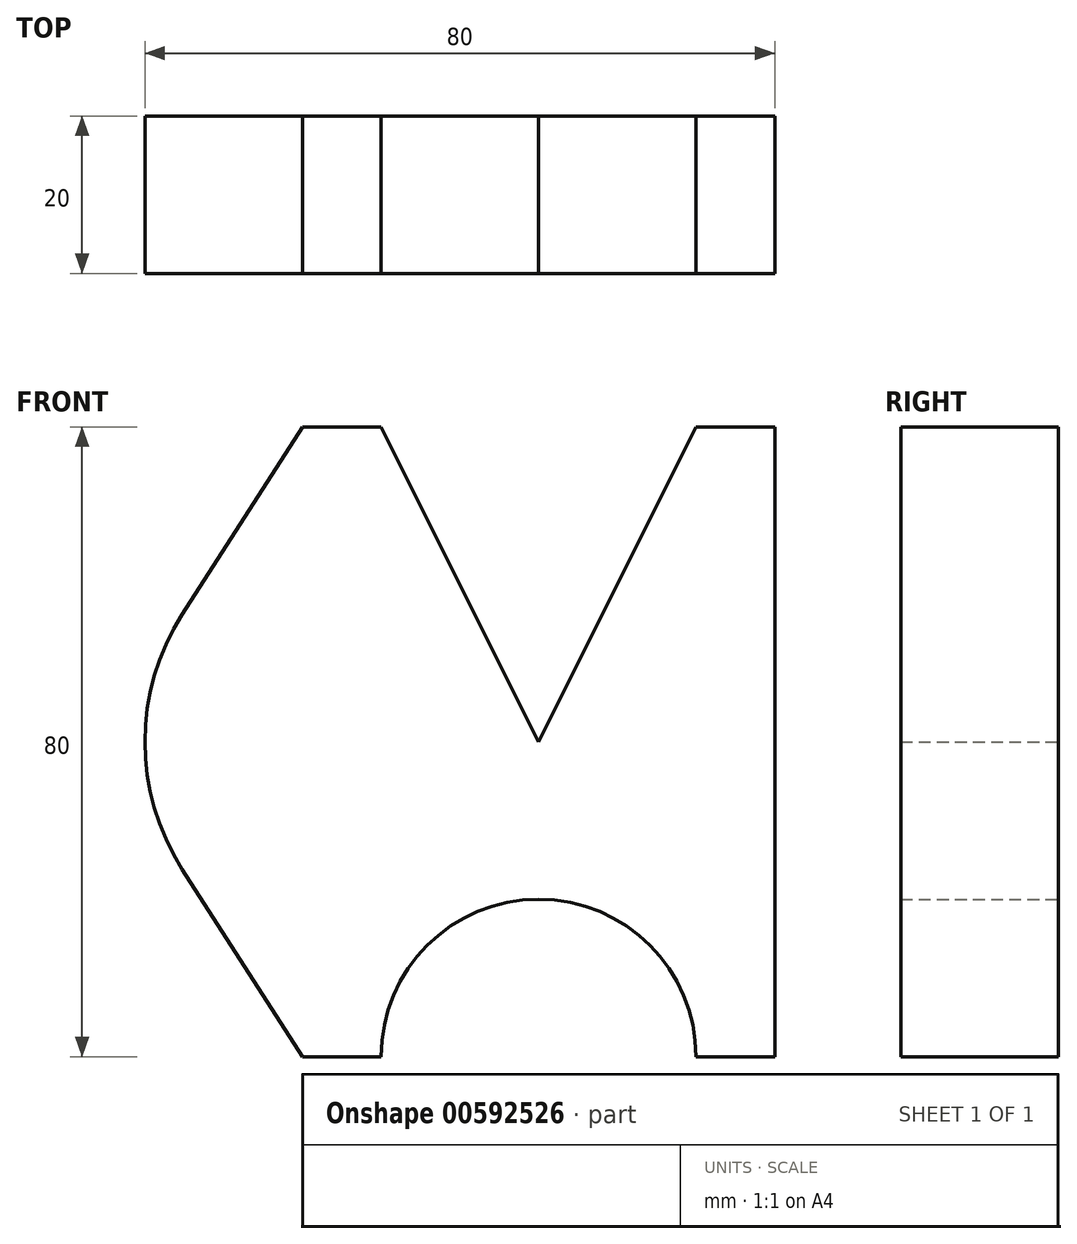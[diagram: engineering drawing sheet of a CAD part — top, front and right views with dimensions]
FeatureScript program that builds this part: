
annotation { "Feature Type Name" : "Feature", "Feature Type Description" : "" }
export const myFeature = defineFeature(function(context is Context, id is Id, definition is map)
    precondition{}
    {
        {
            var Q0;
            Q0=qCreatedBy(makeId("Front.planeOp"),FACE);
            var sketch = newSketch(context, id + "F0", { "sketchPlane" : qUnion([Q0])});
            skLineSegment(sketch, "E0", {"start": v(0, 0) * mm, "end": v(20, 40) * mm});
            skLineSegment(sketch, "E1", {"start": v(20, 40) * mm, "end": v(30, 40) * mm});
            skLineSegment(sketch, "E2", {"start": v(30, 40) * mm, "end": v(30, -40) * mm});
            skLineSegment(sketch, "E3", {"start": v(30, -40) * mm, "end": v(20, -40) * mm});
            skArc(sketch, "E4", {"start": v(20, -40) * mm, "mid": v(0, -20) * mm, "end": v(-20, -40) * mm});
            skLineSegment(sketch, "E5", {"start": v(-20, -40) * mm, "end": v(-30, -40) * mm});
            skLineSegment(sketch, "E6", {"start": v(-30, -40) * mm, "end": v(-45.26, -16.19) * mm});
            skLineSegment(sketch, "E7", {"start": v(0, 0) * mm, "end": v(-20, 40) * mm});
            skLineSegment(sketch, "E8", {"start": v(-20, 40) * mm, "end": v(-30, 40) * mm});
            skLineSegment(sketch, "E9", {"start": v(-30, 40) * mm, "end": v(-45.26, 16.19) * mm});
            skArc(sketch, "E10", {"start": v(-45.26, 16.19) * mm, "mid": v(-50, 0) * mm, "end": v(-45.26, -16.19) * mm});
            skLineSegment(sketch, "E11", {"start": v(-30, 40) * mm, "end": v(-30, -40) * mm, "construction": true});
            skSolve(sketch);
        }
        {
            var Q0;
            Q0=makeQuery(id+"F0.imprint","IMPRINT",FACE,{"disambiguationData":[TD([[makeQuery(id+"F0.imprint","IMPRINT",EDGE,{"derivedFrom":sQuery(id+"F0.wireOp",EDGE,"E0")}),-1.0]])]});
            extrude(context, id + "F1", {"entities" : qUnion([Q0]), "depth" : 20 * mm, "offsetDistance" : 25 * mm});
        }
    });
